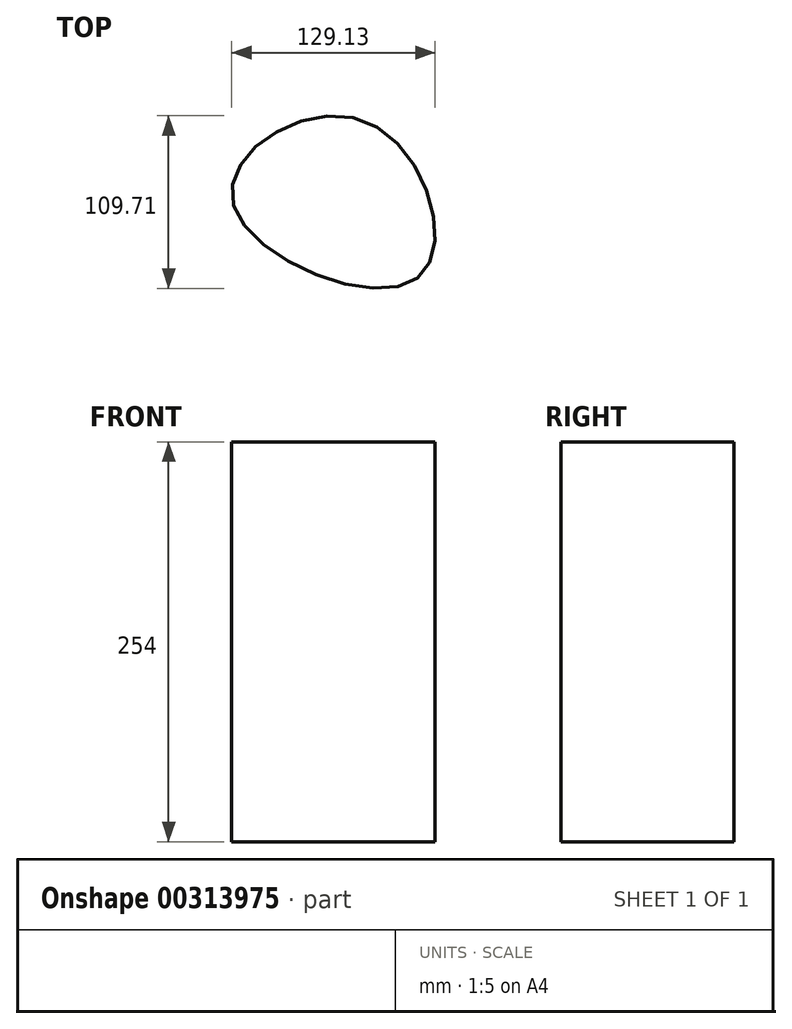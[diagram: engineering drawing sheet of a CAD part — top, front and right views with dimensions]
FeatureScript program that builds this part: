
annotation { "Feature Type Name" : "Feature", "Feature Type Description" : "" }
export const myFeature = defineFeature(function(context is Context, id is Id, definition is map)
    precondition{}
    {
        {
            var Q0;
            Q0=qCreatedBy(makeId("Top.planeOp"),FACE);
            var sketch = newSketch(context, id + "F0", { "sketchPlane" : qUnion([Q0])});
            skFitSpline(sketch, "E0", {"points": [v(59.27, -49.58) * mm, v(-58.2, 0) * mm, v(26.4, 50.11) * mm, v(59.27, -49.58) * mm]});
            skSolve(sketch);
        }
        {
            var Q0;
            Q0 = qSketchRegion(id + "F0", true);
            extrude(context, id + "F1", {"entities" : qUnion([Q0]), "depth" : 254 * mm});
        }
    });
